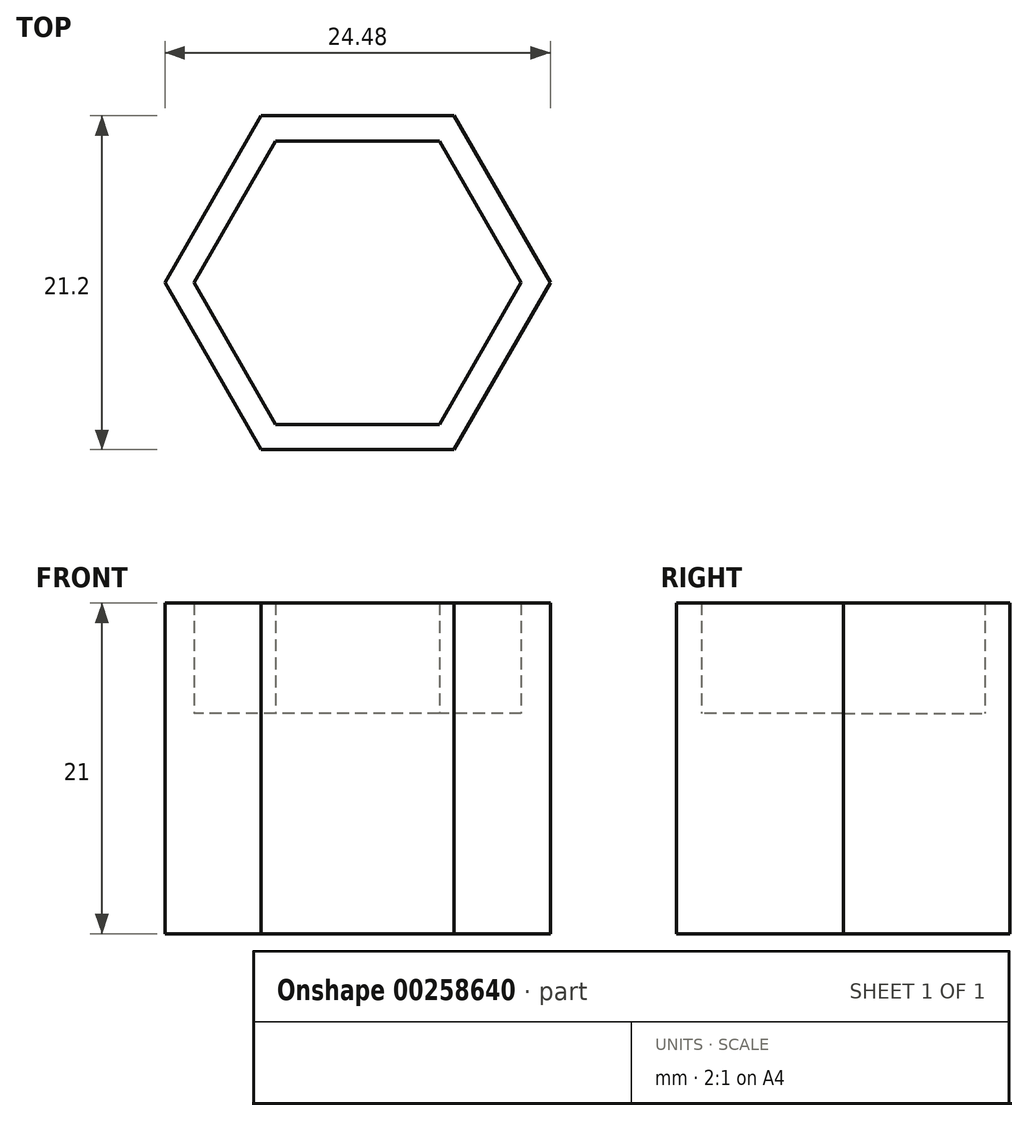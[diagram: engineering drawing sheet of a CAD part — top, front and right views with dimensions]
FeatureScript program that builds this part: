
annotation { "Feature Type Name" : "Feature", "Feature Type Description" : "" }
export const myFeature = defineFeature(function(context is Context, id is Id, definition is map)
    precondition{}
    {
        {
            var Q0;
            Q0=qCreatedBy(makeId("Top.planeOp"),FACE);
            var sketch = newSketch(context, id + "F0", { "sketchPlane" : qUnion([Q0])});
            skCircle(sketch, "E0.cCircle", {"center": v(0, 0.43) * mm, "radius": 9 * mm, "construction": true});
            skLineSegment(sketch, "E0.0", {"start": v(5.2, -8.57) * mm, "end": v(-5.2, -8.57) * mm});
            skLineSegment(sketch, "E0.1", {"start": v(-5.2, -8.57) * mm, "end": v(-10.4, 0.43) * mm});
            skLineSegment(sketch, "E0.2", {"start": v(-10.4, 0.43) * mm, "end": v(-5.2, 9.43) * mm});
            skLineSegment(sketch, "E0.3", {"start": v(-5.2, 9.43) * mm, "end": v(5.2, 9.43) * mm});
            skLineSegment(sketch, "E0.4", {"start": v(5.2, 9.43) * mm, "end": v(10.4, 0.43) * mm});
            skLineSegment(sketch, "E0.5", {"start": v(10.4, 0.43) * mm, "end": v(5.2, -8.57) * mm});
            skPoint(sketch, "E0.0.midPoint", {"position": v(0, -8.57) * mm});
            skLineSegment(sketch, "E1.0", {"start": v(-6.12, -10.17) * mm, "end": v(-12.24, 0.43) * mm});
            skLineSegment(sketch, "E1.1", {"start": v(-6.12, 11.03) * mm, "end": v(6.12, 11.03) * mm});
            skLineSegment(sketch, "E1.2", {"start": v(6.12, 11.03) * mm, "end": v(12.24, 0.43) * mm});
            skLineSegment(sketch, "E1.3", {"start": v(-12.24, 0.43) * mm, "end": v(-6.12, 11.03) * mm});
            skLineSegment(sketch, "E1.4", {"start": v(12.24, 0.43) * mm, "end": v(6.12, -10.17) * mm});
            skLineSegment(sketch, "E1.5", {"start": v(6.12, -10.17) * mm, "end": v(-6.12, -10.17) * mm});
            skSolve(sketch);
        }
        {
            var Q0;
            Q0 = qSketchRegion(id + "F0", true);
            var Q1;
            Q1=makeQuery(id+"F0.imprint","IMPRINT",FACE,{"disambiguationData":[TD([[makeQuery(id+"F0.imprint","IMPRINT",EDGE,{"derivedFrom":sQuery(id+"F0.wireOp",EDGE,"E0.0")}),-1.0]])]});
            extrude(context, id + "F1", {"entities" : qUnion([Q0, Q1]), "oppositeDirection" : true, "depth" : 14 * mm});
        }
        {
            var Q0;
            Q0 = qSketchRegion(id + "F0", true);
            extrude(context, id + "F2", {"entities" : qUnion([Q0]), "operationType" : NewBodyOperationType.ADD, "depth" : 7 * mm});
        }
    });
